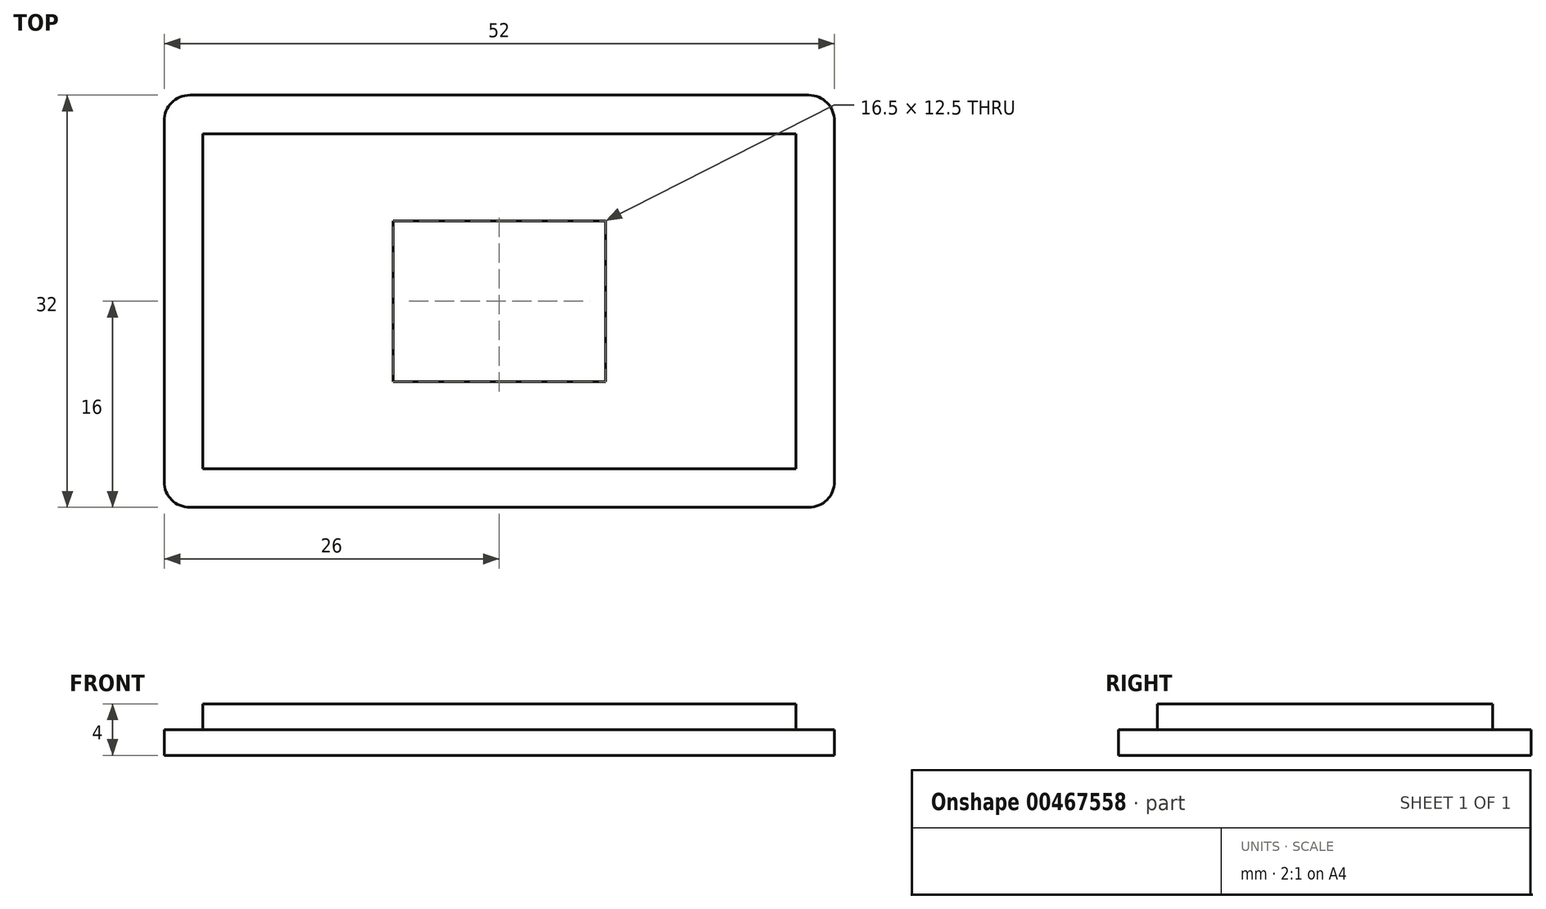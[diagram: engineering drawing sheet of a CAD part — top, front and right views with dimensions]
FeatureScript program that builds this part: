
annotation { "Feature Type Name" : "Feature", "Feature Type Description" : "" }
export const myFeature = defineFeature(function(context is Context, id is Id, definition is map)
    precondition{}
    {
        {
            var Q0;
            Q0=qCreatedBy(makeId("Top.planeOp"),FACE);
            var sketch = newSketch(context, id + "F0", { "sketchPlane" : qUnion([Q0])});
            skLineSegment(sketch, "E0.bottom", {"start": v(-24, 16) * mm, "end": v(24, 16) * mm});
            skLineSegment(sketch, "E0.top", {"start": v(-24, -16) * mm, "end": v(24, -16) * mm});
            skLineSegment(sketch, "E0.left", {"start": v(-26, 14) * mm, "end": v(-26, -14) * mm});
            skLineSegment(sketch, "E0.right", {"start": v(26, 14) * mm, "end": v(26, -14) * mm});
            skPoint(sketch, "E0.middle", {"position": v(0, 0) * mm});
            skPoint(sketch, "E1.visualSharp", {"position": v(-26, 16) * mm});
            skArc(sketch, "E1.filletArc", {"start": v(-24, 16) * mm, "mid": v(-25.41, 15.41) * mm, "end": v(-26, 14) * mm});
            skPoint(sketch, "E2.visualSharp", {"position": v(26, 16) * mm});
            skArc(sketch, "E2.filletArc", {"start": v(26, 14) * mm, "mid": v(25.41, 15.41) * mm, "end": v(24, 16) * mm});
            skPoint(sketch, "E3.visualSharp", {"position": v(-26, -16) * mm});
            skArc(sketch, "E3.filletArc", {"start": v(-26, -14) * mm, "mid": v(-25.41, -15.41) * mm, "end": v(-24, -16) * mm});
            skPoint(sketch, "E4.visualSharp", {"position": v(26, -16) * mm});
            skArc(sketch, "E4.filletArc", {"start": v(24, -16) * mm, "mid": v(25.41, -15.41) * mm, "end": v(26, -14) * mm});
            skArc(sketch, "E5.1", {"start": v(25, 14) * mm, "mid": v(24.7, 14.7) * mm, "end": v(24, 15) * mm});
            skArc(sketch, "E5.2", {"start": v(-24, 15) * mm, "mid": v(-23.3, 13.3) * mm, "end": v(-25, 14) * mm});
            skArc(sketch, "E5.5", {"start": v(-25, -14) * mm, "mid": v(-24.7, -14.7) * mm, "end": v(-24, -15) * mm});
            skArc(sketch, "E5.7", {"start": v(24, -15) * mm, "mid": v(24.7, -14.7) * mm, "end": v(25, -14) * mm});
            skLineSegment(sketch, "E6.bottom", {"start": v(-8.25, 6.25) * mm, "end": v(8.25, 6.25) * mm});
            skLineSegment(sketch, "E6.top", {"start": v(-8.25, -6.25) * mm, "end": v(8.25, -6.25) * mm});
            skLineSegment(sketch, "E6.left", {"start": v(-8.25, 6.25) * mm, "end": v(-8.25, -6.25) * mm});
            skLineSegment(sketch, "E6.right", {"start": v(8.25, 6.25) * mm, "end": v(8.25, -6.25) * mm});
            skLineSegment(sketch, "E7.0", {"start": v(-23, 13) * mm, "end": v(23, 13) * mm});
            skLineSegment(sketch, "E7.1", {"start": v(-23, 13) * mm, "end": v(-23, -13) * mm});
            skLineSegment(sketch, "E7.2", {"start": v(-23, -13) * mm, "end": v(23, -13) * mm});
            skLineSegment(sketch, "E7.3", {"start": v(23, 13) * mm, "end": v(23, -13) * mm});
            skSolve(sketch);
        }
        {
            var Q0;
            Q0=makeQuery(id+"F0.imprint","IMPRINT",FACE,{"disambiguationData":[TD([[makeQuery(id+"F0.imprint","IMPRINT",EDGE,{"derivedFrom":sQuery(id+"F0.wireOp",EDGE,"E6.bottom")}),1.0]])]});
            extrude(context, id + "F1", {"entities" : qUnion([Q0]), "depth" : 4 * mm});
        }
        {
            var Q0;
            Q0 = qSketchRegion(id + "F0", true);
            extrude(context, id + "F2", {"entities" : qUnion([Q0]), "operationType" : NewBodyOperationType.ADD, "depth" : 2 * mm});
        }
    });
